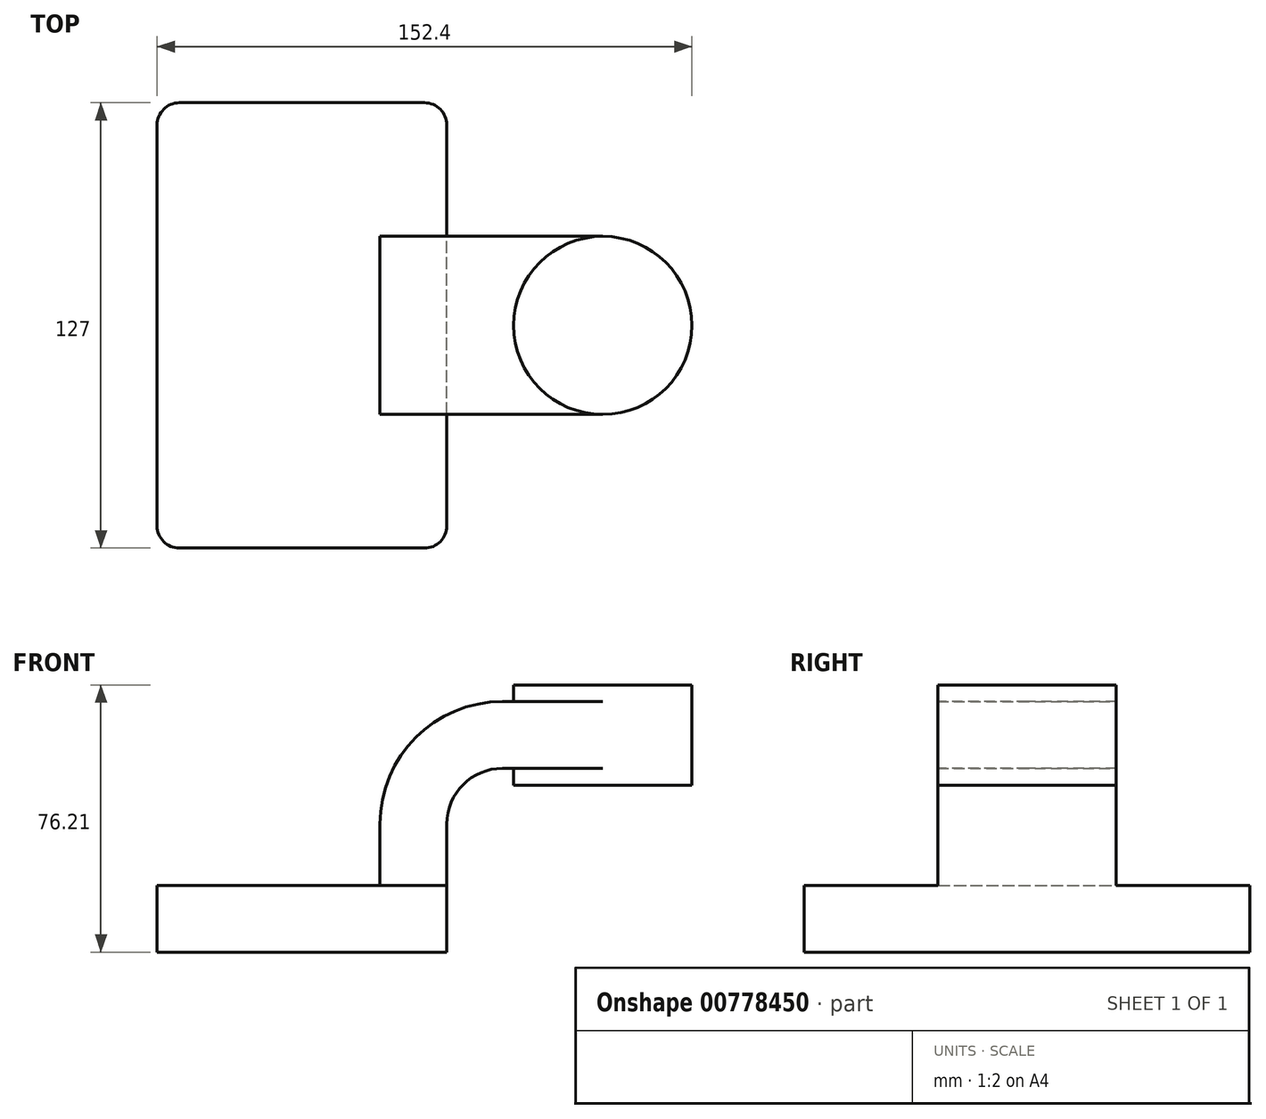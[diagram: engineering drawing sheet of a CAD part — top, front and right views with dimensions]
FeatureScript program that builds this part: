
annotation { "Feature Type Name" : "Feature", "Feature Type Description" : "" }
export const myFeature = defineFeature(function(context is Context, id is Id, definition is map)
    precondition{}
    {
        {
            var Q0;
            Q0=qCreatedBy(makeId("Front.planeOp"),FACE);
            var sketch = newSketch(context, id + "F0", { "sketchPlane" : qUnion([Q0])});
            skLineSegment(sketch, "E0.bottom", {"start": v(41.27, 9.53) * mm, "end": v(-41.28, 9.53) * mm});
            skLineSegment(sketch, "E0.top", {"start": v(41.28, -9.52) * mm, "end": v(-41.27, -9.52) * mm});
            skLineSegment(sketch, "E0.left", {"start": v(41.28, 9.53) * mm, "end": v(41.28, -9.52) * mm});
            skLineSegment(sketch, "E0.right", {"start": v(-41.28, 9.53) * mm, "end": v(-41.27, -9.52) * mm});
            skPoint(sketch, "E0.middle", {"position": v(0, 0) * mm});
            skLineSegment(sketch, "E1.bottom", {"start": v(60.33, 38.1) * mm, "end": v(111.12, 38.1) * mm});
            skLineSegment(sketch, "E1.top", {"start": v(60.32, 66.68) * mm, "end": v(111.12, 66.68) * mm});
            skLineSegment(sketch, "E1.left", {"start": v(60.33, 38.1) * mm, "end": v(60.32, 66.67) * mm});
            skLineSegment(sketch, "E1.right", {"start": v(111.13, 38.1) * mm, "end": v(111.12, 66.68) * mm});
            skPoint(sketch, "E1.middle", {"position": v(85.72, 52.39) * mm});
            skLineSegment(sketch, "E2", {"start": v(41.27, 9.53) * mm, "end": v(41.27, 27) * mm});
            skArc(sketch, "E3", {"start": v(41.27, 27) * mm, "mid": v(45.92, 38.23) * mm, "end": v(57.15, 42.88) * mm});
            skLineSegment(sketch, "E4", {"start": v(57.15, 42.88) * mm, "end": v(85.72, 42.88) * mm});
            skLineSegment(sketch, "E5.0", {"start": v(57.15, 61.93) * mm, "end": v(85.72, 61.93) * mm});
            skArc(sketch, "E5.1", {"start": v(22.23, 27) * mm, "mid": v(32.45, 51.7) * mm, "end": v(57.15, 61.93) * mm});
            skLineSegment(sketch, "E5.2", {"start": v(22.22, 9.53) * mm, "end": v(22.22, 27) * mm});
            skFitSpline(sketch, "E6", {"points": [v(-41.28, 9.52) * mm, v(57.15, 61.93) * mm], "startDerivative": vector(-6.93, 98.5) * mm, "endDerivative": vector(72.92, -11.4) * mm});
            skLineSegment(sketch, "E7", {"start": v(85.72, 38.1) * mm, "end": v(85.72, 66.68) * mm});
            skSolve(sketch);
        }
        {
            var Q0;
            Q0=makeQuery(id+"F0.imprint","IMPRINT",FACE,{"disambiguationData":[TD([[makeQuery(id+"F0.imprint","IMPRINT",EDGE,{"derivedFrom":sQuery(id+"F0.wireOp",EDGE,"E0.top")}),-1.0]])]});
            extrude(context, id + "F1", {"entities" : qUnion([Q0]), "endBound" : BoundingType.SYMMETRIC, "depth" : 127 * mm, "offsetDistance" : 25.4 * mm});
        }
        {
            var Q0;
            {var subQ1=sQuery(id+"F0.wireOp",EDGE,"E2");Q0=makeQuery(id+"F0.imprint","IMPRINT",FACE,{"disambiguationData":[TD([[makeQuery(id+"F0.imprint","IMPRINT",EDGE,{"derivedFrom":subQ1}),1.0]])]});}
            var Q1;
            {var subQ0=sQuery(id+"F0.wireOp",EDGE,"E4");var subQ1=sQuery(id+"F0.wireOp",EDGE,"E1.left");var subQ2=makeQuery(id+"F0.imprint","INTERSECT",VERTEX,{"derivedFrom":[subQ1,subQ0]});Q1=makeQuery(id+"F0.imprint","IMPRINT",FACE,{"disambiguationData":[TD([[makeQuery(id+"F0.imprint","IMPRINT",EDGE,{"disambiguationData":[TD([[subQ2,-1.0]])],"derivedFrom":subQ1}),-1.0]])]});}
            extrude(context, id + "F2", {"entities" : qUnion([Q0, Q1]), "operationType" : NewBodyOperationType.ADD, "endBound" : BoundingType.SYMMETRIC, "depth" : 50.8 * mm, "offsetDistance" : 25.4 * mm});
        }
        {
            var Q0;
            {var subQ4=sQuery(id+"F0.wireOp",EDGE,"E1.right");Q0=makeQuery(id+"F0.imprint","IMPRINT",FACE,{"disambiguationData":[TD([[makeQuery(id+"F0.imprint","IMPRINT",EDGE,{"derivedFrom":subQ4}),1.0]])]});}
            var Q1;
            Q1=sQuery(id+"F0.wireOp",EDGE,"E7");
            revolve(context, id + "F3", {"operationType" : NewBodyOperationType.ADD, "surfaceOperationType" : NewSurfaceOperationType.NEW, "entities" : qUnion([Q0]), "axis" : qUnion([Q1]), "revolveType" : RevolveType.FULL});
        }
        {
            var Q0;
            Q0=makeQuery(id+"F1.opExtrude","CAP_EDGE",EDGE,{"disambiguationData":[OSD([sQuery(id+"F0.wireOp",EDGE,"E0.left")])],"isStart":false});
            var Q1;
            Q1=makeQuery(id+"F1.opExtrude","CAP_EDGE",EDGE,{"disambiguationData":[OSD([sQuery(id+"F0.wireOp",EDGE,"E0.right")])],"isStart":false});
            var Q2;
            Q2=makeQuery(id+"F1.opExtrude","CAP_EDGE",EDGE,{"disambiguationData":[OSD([sQuery(id+"F0.wireOp",EDGE,"E0.right")])],"isStart":true});
            var Q3;
            Q3=makeQuery(id+"F1.opExtrude","CAP_EDGE",EDGE,{"disambiguationData":[OSD([sQuery(id+"F0.wireOp",EDGE,"E0.left")])],"isStart":true});
            fillet(context, id + "F4", {"entities" : qUnion([Q0, Q1, Q2, Q3]), "radius" : 6.35 * mm, "tangentPropagation" : true, "allowEdgeOverflow" : false});
        }
        {
            var Q0;
            Q0=makeQuery(id+"F0.imprint","IMPRINT",FACE,{"disambiguationData":[TD([[makeQuery(id+"F0.imprint","IMPRINT",EDGE,{"derivedFrom":sQuery(id+"F0.wireOp",EDGE,"E5.1")}),1.0]])]});
            extrude(context, id + "F5", {"entities" : qUnion([Q0]), "operationType" : NewBodyOperationType.ADD, "endBound" : BoundingType.SYMMETRIC, "depth" : 15.88 * mm, "offsetDistance" : 25.4 * mm});
        }
    });
